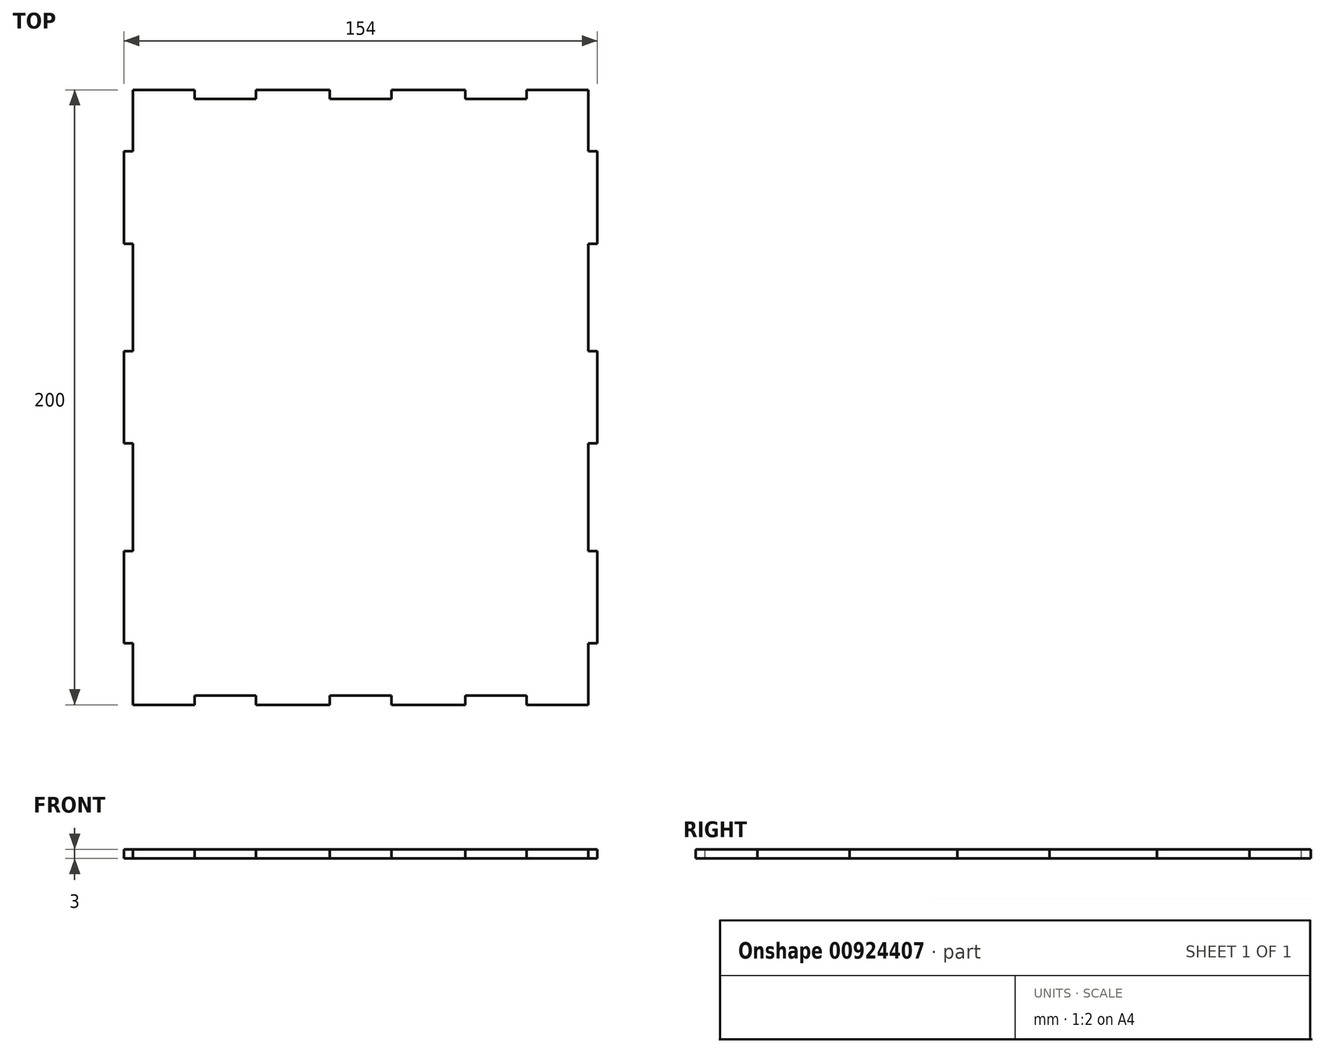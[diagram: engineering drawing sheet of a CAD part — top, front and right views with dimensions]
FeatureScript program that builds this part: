
annotation { "Feature Type Name" : "Feature", "Feature Type Description" : "" }
export const myFeature = defineFeature(function(context is Context, id is Id, definition is map)
    precondition{}
    {
        {
            var Q0;
            Q0=qCreatedBy(makeId("Top.planeOp"),FACE);
            var sketch = newSketch(context, id + "F0", { "sketchPlane" : qUnion([Q0])});
            skLineSegment(sketch, "E0.bottom", {"start": v(0, 0) * mm, "end": v(74, 0) * mm});
            skLineSegment(sketch, "E0.top", {"start": v(0, 200) * mm, "end": v(74, 200) * mm});
            skLineSegment(sketch, "E0.left", {"start": v(0, 0) * mm, "end": v(0, 200) * mm, "construction": true});
            skLineSegment(sketch, "E0.right", {"start": v(74, 0) * mm, "end": v(74, 20) * mm});
            skLineSegment(sketch, "E1.bottom", {"start": v(74, 20) * mm, "end": v(77, 20) * mm});
            skLineSegment(sketch, "E1.top", {"start": v(74, 50) * mm, "end": v(77, 50) * mm});
            skLineSegment(sketch, "E1.right", {"start": v(77, 20) * mm, "end": v(77, 50) * mm});
            skLineSegment(sketch, "E2.trimOffspring", {"start": v(74, 50) * mm, "end": v(74, 85) * mm});
            skLineSegment(sketch, "E3.bottom", {"start": v(74, 115) * mm, "end": v(77, 115) * mm});
            skLineSegment(sketch, "E3.top", {"start": v(74, 85) * mm, "end": v(77, 85) * mm});
            skLineSegment(sketch, "E3.right", {"start": v(77, 115) * mm, "end": v(77, 85) * mm});
            skLineSegment(sketch, "E4.trimOffspring", {"start": v(74, 115) * mm, "end": v(74, 150) * mm});
            skLineSegment(sketch, "E5.bottom", {"start": v(74, 180) * mm, "end": v(77, 180) * mm});
            skLineSegment(sketch, "E5.top", {"start": v(74, 150) * mm, "end": v(77, 150) * mm});
            skLineSegment(sketch, "E5.right", {"start": v(77, 180) * mm, "end": v(77, 150) * mm});
            skLineSegment(sketch, "E6.trimOffspring", {"start": v(74, 180) * mm, "end": v(74, 200) * mm});
            skLineSegment(sketch, "E7.MirrorCS", {"start": v(-74, 50) * mm, "end": v(-77, 50) * mm});
            skLineSegment(sketch, "E8.MirrorCS", {"start": v(-74, 20) * mm, "end": v(-77, 20) * mm});
            skLineSegment(sketch, "E9.MirrorCS", {"start": v(-74, 85) * mm, "end": v(-77, 85) * mm});
            skLineSegment(sketch, "E10.MirrorCS", {"start": v(-74, 115) * mm, "end": v(-77, 115) * mm});
            skLineSegment(sketch, "E11.MirrorCS", {"start": v(-74, 150) * mm, "end": v(-77, 150) * mm});
            skLineSegment(sketch, "E12.MirrorCS", {"start": v(-74, 180) * mm, "end": v(-77, 180) * mm});
            skLineSegment(sketch, "E13.MirrorCS", {"start": v(-77, 115) * mm, "end": v(-77, 85) * mm});
            skLineSegment(sketch, "E14.MirrorCS", {"start": v(-77, 20) * mm, "end": v(-77, 50) * mm});
            skLineSegment(sketch, "E15.MirrorCS", {"start": v(-77, 180) * mm, "end": v(-77, 150) * mm});
            skLineSegment(sketch, "E16.MirrorCS", {"start": v(-74, 50) * mm, "end": v(-74, 85) * mm});
            skLineSegment(sketch, "E17.MirrorCS", {"start": v(0, 0) * mm, "end": v(-74, 0) * mm});
            skLineSegment(sketch, "E18.MirrorCS", {"start": v(0, 200) * mm, "end": v(-74, 200) * mm});
            skLineSegment(sketch, "E19.MirrorCS", {"start": v(-74, 115) * mm, "end": v(-74, 150) * mm});
            skLineSegment(sketch, "E20.MirrorCS", {"start": v(-74, 180) * mm, "end": v(-74, 200) * mm});
            skLineSegment(sketch, "E21.MirrorCS", {"start": v(-74, 0) * mm, "end": v(-74, 20) * mm});
            skSolve(sketch);
        }
        {
            var Q0;
            Q0=makeQuery(id+"F0.imprint","IMPRINT",FACE,{"disambiguationData":[TD([[makeQuery(id+"F0.imprint","IMPRINT",EDGE,{"derivedFrom":sQuery(id+"F0.wireOp",EDGE,"WMlABEH4-TAOB-4h2d-YXed-Et6fKAML2MZI.bottom")}),1.0]])]});
            var Q1;
            Q1=makeQuery(id+"F0.imprint","IMPRINT",FACE,{"disambiguationData":[TD([[makeQuery(id+"F0.imprint","IMPRINT",EDGE,{"derivedFrom":sQuery(id+"F0.wireOp",EDGE,"E0.bottom")}),1.0]])]});
            extrude(context, id + "F1", {"entities" : qUnion([Q0, Q1]), "depth" : 3 * mm, "offsetDistance" : 25 * mm});
        }
        {
            var Q0;
            Q0=makeQuery(id+"F1.opExtrude","CAP_FACE",FACE,{"disambiguationData":[OSD([sQuery(id+"F0.wireOp",EDGE,"E0.bottom"),sQuery(id+"F0.wireOp",EDGE,"E0.top"),sQuery(id+"F0.wireOp",EDGE,"E0.right"),sQuery(id+"F0.wireOp",EDGE,"E1.bottom"),sQuery(id+"F0.wireOp",EDGE,"E1.top"),sQuery(id+"F0.wireOp",EDGE,"E1.right"),sQuery(id+"F0.wireOp",EDGE,"E2.trimOffspring"),sQuery(id+"F0.wireOp",EDGE,"E3.bottom"),sQuery(id+"F0.wireOp",EDGE,"E3.top"),sQuery(id+"F0.wireOp",EDGE,"E3.right"),sQuery(id+"F0.wireOp",EDGE,"E4.trimOffspring"),sQuery(id+"F0.wireOp",EDGE,"E5.bottom"),sQuery(id+"F0.wireOp",EDGE,"E5.top"),sQuery(id+"F0.wireOp",EDGE,"E5.right"),sQuery(id+"F0.wireOp",EDGE,"E6.trimOffspring"),sQuery(id+"F0.wireOp",EDGE,"E7.MirrorCS"),sQuery(id+"F0.wireOp",EDGE,"E8.MirrorCS"),sQuery(id+"F0.wireOp",EDGE,"E9.MirrorCS"),sQuery(id+"F0.wireOp",EDGE,"E10.MirrorCS"),sQuery(id+"F0.wireOp",EDGE,"E11.MirrorCS"),sQuery(id+"F0.wireOp",EDGE,"E12.MirrorCS"),sQuery(id+"F0.wireOp",EDGE,"E13.MirrorCS"),sQuery(id+"F0.wireOp",EDGE,"E14.MirrorCS"),sQuery(id+"F0.wireOp",EDGE,"E15.MirrorCS"),sQuery(id+"F0.wireOp",EDGE,"E16.MirrorCS"),sQuery(id+"F0.wireOp",EDGE,"E17.MirrorCS"),sQuery(id+"F0.wireOp",EDGE,"E18.MirrorCS"),sQuery(id+"F0.wireOp",EDGE,"E19.MirrorCS"),sQuery(id+"F0.wireOp",EDGE,"E20.MirrorCS"),sQuery(id+"F0.wireOp",EDGE,"E21.MirrorCS")])],"isStart":false});
            var sketch = newSketch(context, id + "F2", { "sketchPlane" : qUnion([Q0])});
            skLineSegment(sketch, "E22.bottom", {"start": v(-54, 0) * mm, "end": v(-34, 0) * mm});
            skLineSegment(sketch, "E22.top", {"start": v(-54, 3) * mm, "end": v(-34, 3) * mm});
            skLineSegment(sketch, "E22.left", {"start": v(-54, 0) * mm, "end": v(-54, 3) * mm});
            skLineSegment(sketch, "E22.right", {"start": v(-34, 0) * mm, "end": v(-34, 3) * mm});
            skLineSegment(sketch, "E23.bottom", {"start": v(34, 0) * mm, "end": v(54, 0) * mm});
            skLineSegment(sketch, "E23.top", {"start": v(34, 3) * mm, "end": v(54, 3) * mm});
            skLineSegment(sketch, "E23.left", {"start": v(34, 0) * mm, "end": v(34, 3) * mm});
            skLineSegment(sketch, "E23.right", {"start": v(54, 0) * mm, "end": v(54, 3) * mm});
            skLineSegment(sketch, "E24.bottom", {"start": v(10, 0) * mm, "end": v(-10, 0) * mm});
            skLineSegment(sketch, "E24.top", {"start": v(10, 3) * mm, "end": v(-10, 3) * mm});
            skLineSegment(sketch, "E24.left", {"start": v(10, 0) * mm, "end": v(10, 3) * mm});
            skLineSegment(sketch, "E24.right", {"start": v(-10, 0) * mm, "end": v(-10, 3) * mm});
            skLineSegment(sketch, "E25", {"start": v(-34, 1.5) * mm, "end": v(-10, 1.5) * mm, "construction": true});
            skLineSegment(sketch, "E26", {"start": v(10, 1.5) * mm, "end": v(34, 1.5) * mm, "construction": true});
            skLineSegment(sketch, "E27", {"start": v(-77, 100) * mm, "end": v(77, 100) * mm, "construction": true});
            skLineSegment(sketch, "E28.MirrorCS", {"start": v(-34, 200) * mm, "end": v(-34, 197) * mm});
            skLineSegment(sketch, "E29.MirrorCS", {"start": v(34, 200) * mm, "end": v(34, 197) * mm});
            skLineSegment(sketch, "E30.MirrorCS", {"start": v(54, 200) * mm, "end": v(54, 197) * mm});
            skLineSegment(sketch, "E31.MirrorCS", {"start": v(-10, 200) * mm, "end": v(-10, 197) * mm});
            skLineSegment(sketch, "E32.MirrorCS", {"start": v(10, 200) * mm, "end": v(10, 197) * mm});
            skLineSegment(sketch, "E33.MirrorCS", {"start": v(-54, 200) * mm, "end": v(-54, 197) * mm});
            skLineSegment(sketch, "E34.MirrorCS", {"start": v(-54, 197) * mm, "end": v(-34, 197) * mm});
            skLineSegment(sketch, "E35.MirrorCS", {"start": v(34, 197) * mm, "end": v(54, 197) * mm});
            skLineSegment(sketch, "E36.MirrorCS", {"start": v(34, 200) * mm, "end": v(54, 200) * mm});
            skLineSegment(sketch, "E37.MirrorCS", {"start": v(-54, 200) * mm, "end": v(-34, 200) * mm});
            skLineSegment(sketch, "E38.MirrorCS", {"start": v(10, 200) * mm, "end": v(-10, 200) * mm});
            skLineSegment(sketch, "E39.MirrorCS", {"start": v(10, 197) * mm, "end": v(-10, 197) * mm});
            skLineSegment(sketch, "E40.MirrorCS", {"start": v(-34, 198.5) * mm, "end": v(-10, 198.5) * mm, "construction": true});
            skLineSegment(sketch, "E41.MirrorCS", {"start": v(10, 198.5) * mm, "end": v(34, 198.5) * mm, "construction": true});
            skSolve(sketch);
        }
        {
            var Q0;
            Q0 = qSketchRegion(id + "F2", true);
            extrude(context, id + "F3", {"entities" : qUnion([Q0]), "operationType" : NewBodyOperationType.REMOVE, "endBound" : BoundingType.THROUGH_ALL, "oppositeDirection" : true, "depth" : 25 * mm, "offsetDistance" : 25 * mm});
        }
    });
